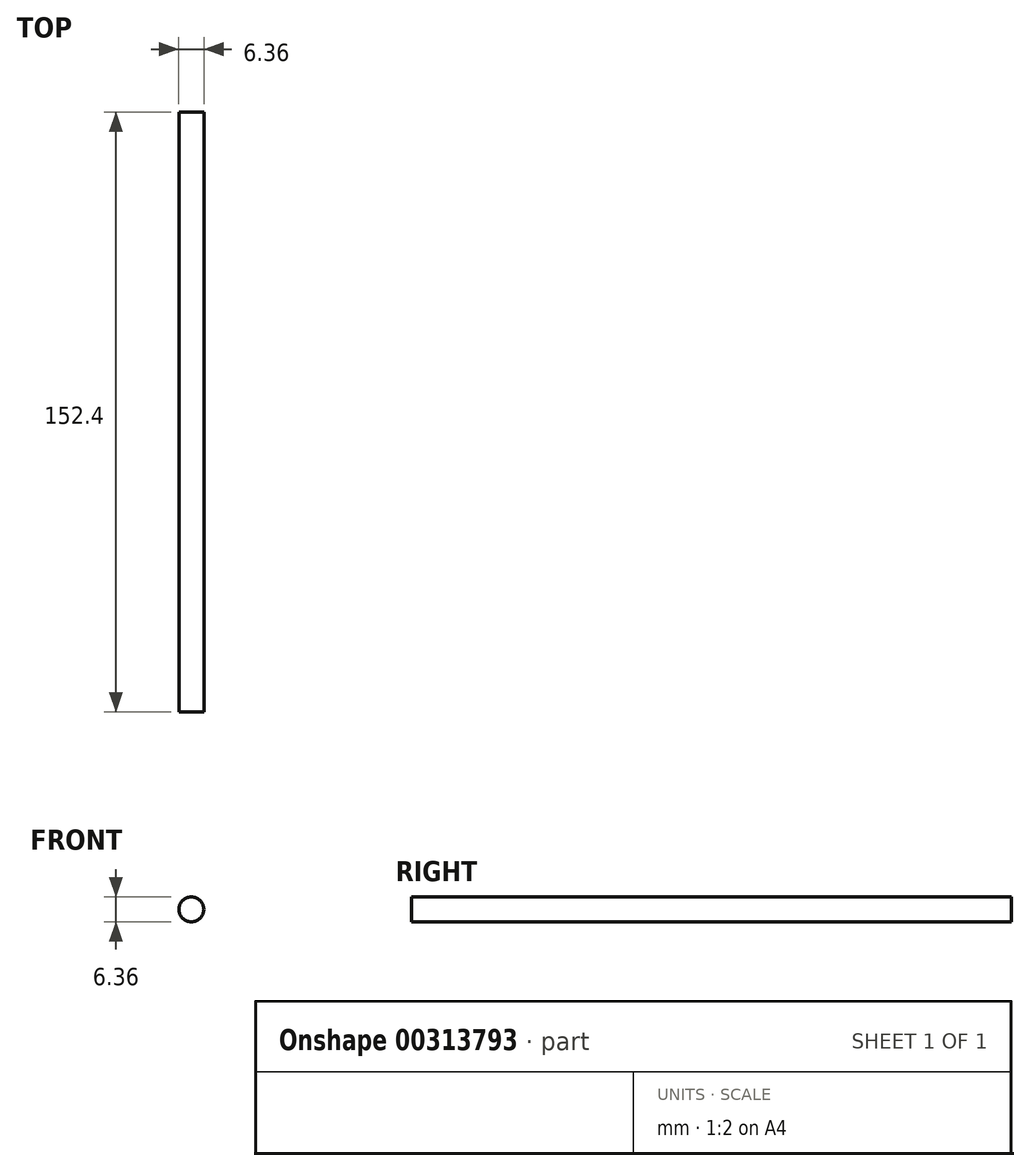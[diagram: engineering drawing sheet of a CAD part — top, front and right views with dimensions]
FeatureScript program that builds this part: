
annotation { "Feature Type Name" : "Feature", "Feature Type Description" : "" }
export const myFeature = defineFeature(function(context is Context, id is Id, definition is map)
    precondition{}
    {
        {
            var Q0;
            Q0=qCreatedBy(makeId("Front.planeOp"),FACE);
            var sketch = newSketch(context, id + "F0", { "sketchPlane" : qUnion([Q0])});
            skCircle(sketch, "E0", {"center": v(0, 0) * mm, "radius": 3.18 * mm});
            skSolve(sketch);
        }
        {
            var Q0;
            Q0 = qSketchRegion(id + "F0", true);
            extrude(context, id + "F1", {"entities" : qUnion([Q0]), "endBound" : BoundingType.SYMMETRIC, "depth" : 152.4 * mm});
        }
    });
